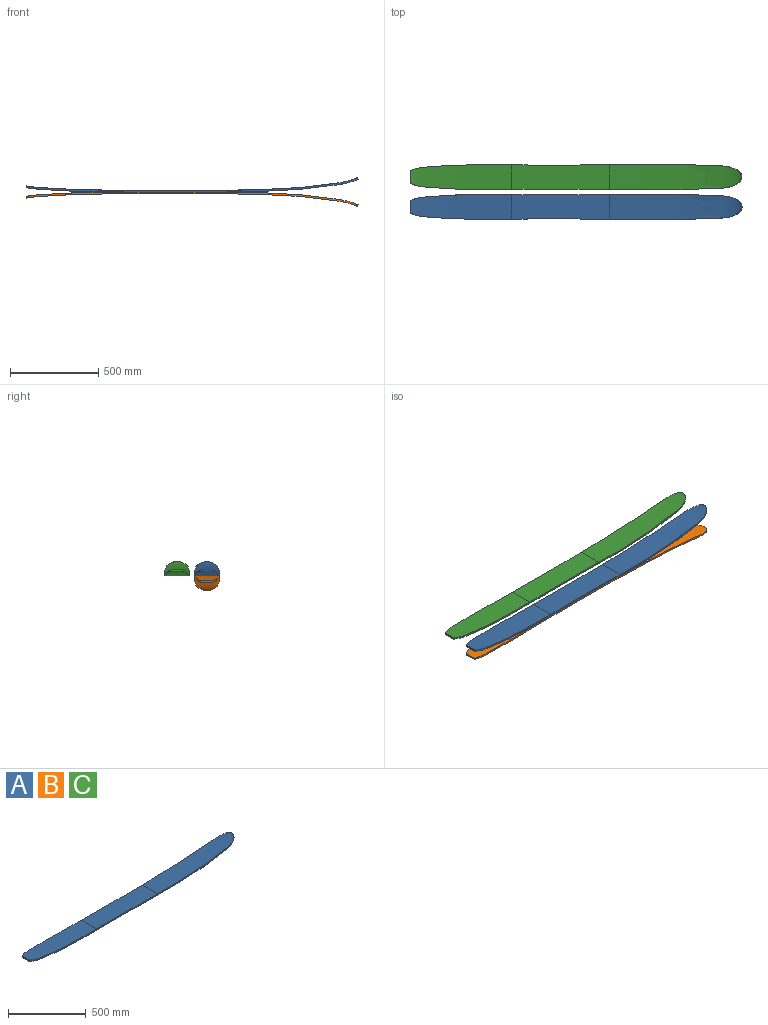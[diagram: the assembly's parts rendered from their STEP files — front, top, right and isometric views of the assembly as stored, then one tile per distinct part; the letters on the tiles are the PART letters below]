
ASSEMBLY  parts=3 mates=1
PART A: 22 faces, bbox 1880x144x81.7 mm
  f0: bspline ~75.89x18.4mm, area 777mm2, adj f1,f15,f16,f19
  f1: bspline ~10.83x9.1mm, area 114.5mm2, adj f0,f2,f16,f19
  f2: plane 57.19x9.85mm, normal (-0.98,0,0.17), area 571.9mm2, adj f1,f3,f16,f19
  f3: bspline ~10.83x9.1mm, area 114.5mm2, adj f2,f4,f16,f19
  f4: bspline ~75.89x18.4mm, area 777mm2, adj f3,f5,f16,f19
  f5: bspline ~333.05x23.69mm, area 3333.4mm2, adj f4,f6,f16,f19
  f6: bspline ~162.61x11.3mm, area 1625.4mm2, adj f5,f7,f16,f19
  f7: cylinder r=40847.54mm len=553.57mm, axis (0,0,1), area 5535.7mm2, adj f6,f8,f17,f20
  f8: bspline ~200.11x13.18mm, area 2000mm2, adj f7,f9,f18,f21
  f9: bspline ~443.46x48.51mm, area 4446mm2, adj f8,f10,f18,f21
  f10: bspline ~124.91x108.58mm, area 2727.4mm2, adj f9,f11,f18,f21
  f11: bspline ~443.46x48.51mm, area 4446mm2, adj f10,f12,f18,f21
  f12: bspline ~200.11x13.18mm, area 2000mm2, adj f11,f13,f18,f21
  f13: cylinder r=40847.54mm len=553.57mm, axis (0,0,1), area 5535.7mm2, adj f12,f14,f17,f20
  f14: bspline ~162.61x11.3mm, area 1625.4mm2, adj f13,f15,f16,f19
  f15: bspline ~333.05x23.69mm, area 3333.4mm2, adj f0,f14,f16,f19
  f16: extruded ~574.7x140mm, area 74109.7mm2, adj f0,f1,f2,f3,f4,f5,f6,f14
  f17: plane 553.57x138.64mm, normal (0,0,1), area 75667.3mm2, adj f7,f13,f16,f18
  f18: extruded ~745.01x142.84mm, area 97856mm2, adj f8,f9,f10,f11,f12,f17
  f19: extruded ~576.43x140mm, area 74103.2mm2, adj f0,f1,f2,f3,f4,f5,f6,f14
  f20: plane 553.57x138.64mm, normal (0,0,-1), area 75667.3mm2, adj f7,f13,f19,f21
  f21: extruded ~750x142.84mm, area 98666.2mm2, adj f8,f9,f10,f11,f12,f20
PART B: same geometry as A
PART C: same geometry as A
PLACE A t=(-197.92,-396.4,164.84)mm
PLACE B rot(axis=(1,0,0),180deg) t=(-197.92,-396.4,-15.16)mm
PLACE C t=(-197.95,-227.29,165.16)mm
MATE fastened B.f20 <-> A.f20  axis (0,0,1) through (-764.23,-396.4,74.84)mm
